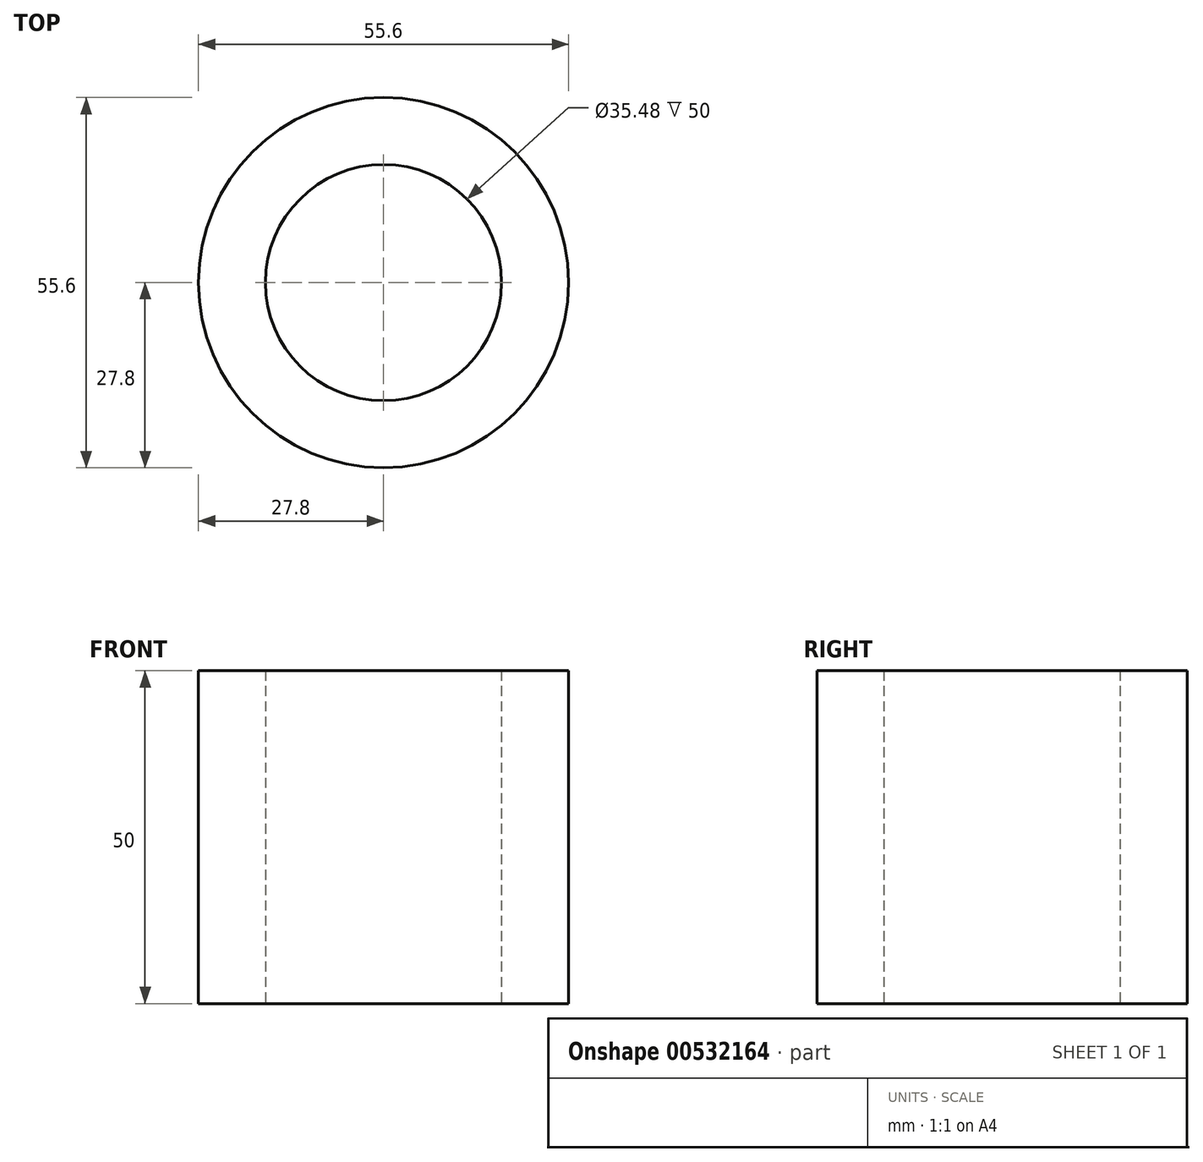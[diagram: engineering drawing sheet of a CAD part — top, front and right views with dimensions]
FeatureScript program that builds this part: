
annotation { "Feature Type Name" : "Feature", "Feature Type Description" : "" }
export const myFeature = defineFeature(function(context is Context, id is Id, definition is map)
    precondition{}
    {
        {
            var Q0;
            Q0=qCreatedBy(makeId("Top.planeOp"),FACE);
            var sketch = newSketch(context, id + "F0", { "sketchPlane" : qUnion([Q0])});
            skCircle(sketch, "E0", {"center": v(0, 0) * mm, "radius": 17.74 * mm});
            skCircle(sketch, "E1", {"center": v(0, 0) * mm, "radius": 27.8 * mm});
            skSolve(sketch);
        }
        {
            var Q0;
            Q0 = qSketchRegion(id + "F0", true);
            extrude(context, id + "F1", {"entities" : qUnion([Q0]), "depth" : 50 * mm, "offsetDistance" : 25 * mm});
        }
    });
